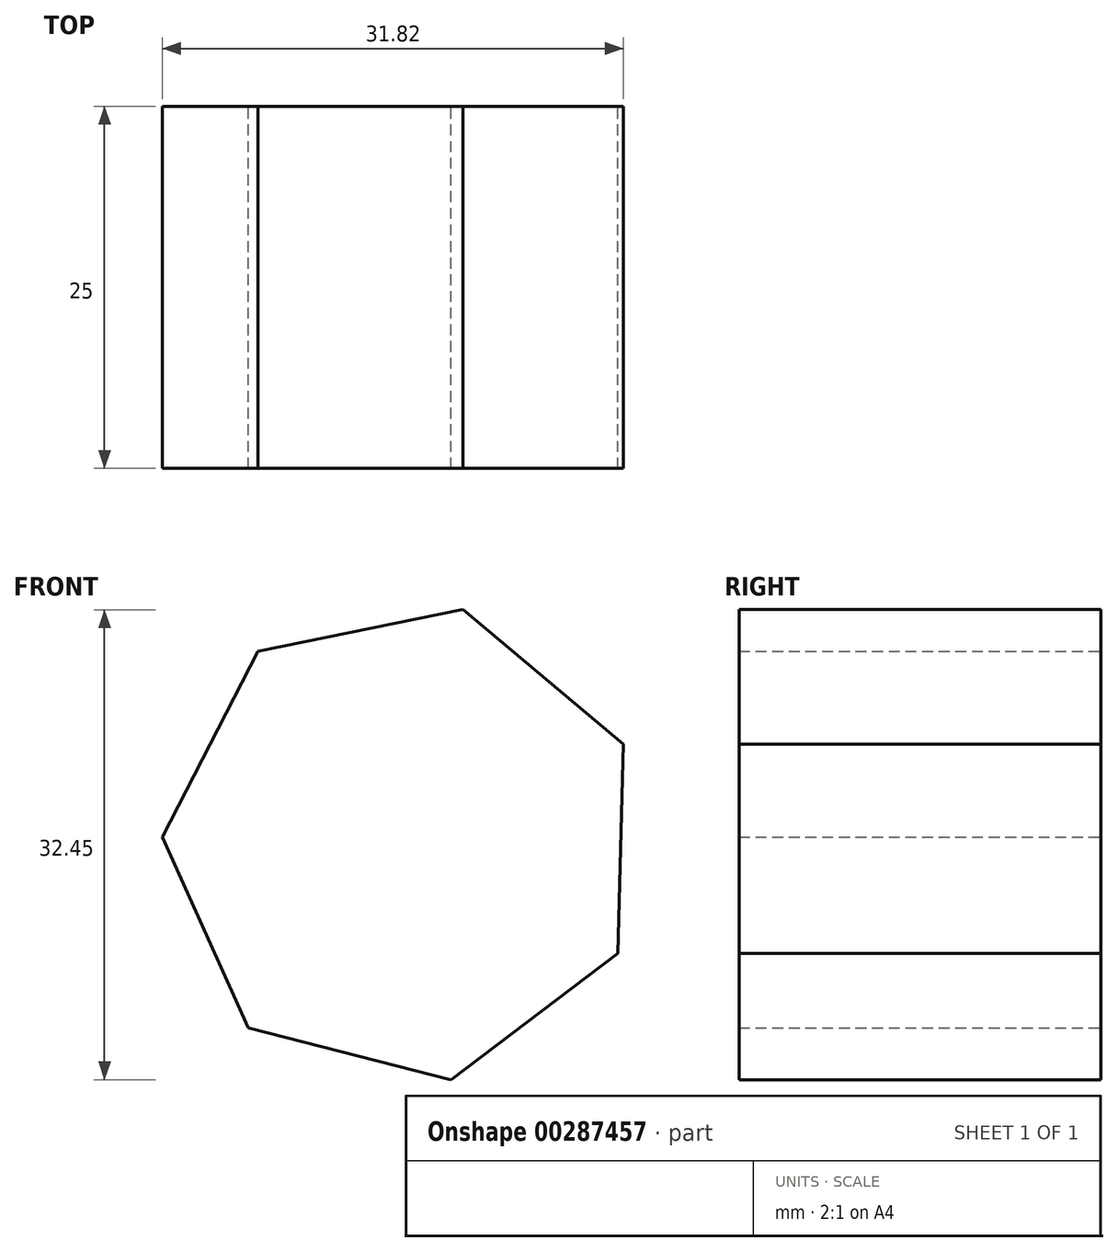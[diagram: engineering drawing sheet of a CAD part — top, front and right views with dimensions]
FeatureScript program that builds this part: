
annotation { "Feature Type Name" : "Feature", "Feature Type Description" : "" }
export const myFeature = defineFeature(function(context is Context, id is Id, definition is map)
    precondition{}
    {
        {
            var Q0;
            Q0=qCreatedBy(makeId("Front.planeOp"),FACE);
            var sketch = newSketch(context, id + "F0", { "sketchPlane" : qUnion([Q0])});
            skCircle(sketch, "E0.cCircle", {"center": v(0, 0) * mm, "radius": 15 * mm, "construction": true});
            skLineSegment(sketch, "E0.0", {"start": v(4.1, 16.13) * mm, "end": v(15.18, 6.85) * mm});
            skLineSegment(sketch, "E0.1", {"start": v(15.18, 6.85) * mm, "end": v(14.81, -7.6) * mm});
            skLineSegment(sketch, "E0.2", {"start": v(14.81, -7.6) * mm, "end": v(3.3, -16.32) * mm});
            skLineSegment(sketch, "E0.3", {"start": v(3.3, -16.32) * mm, "end": v(-10.7, -12.75) * mm});
            skLineSegment(sketch, "E0.4", {"start": v(-10.7, -12.75) * mm, "end": v(-16.64, 0.42) * mm});
            skLineSegment(sketch, "E0.5", {"start": v(-16.64, 0.42) * mm, "end": v(-10.05, 13.27) * mm});
            skLineSegment(sketch, "E0.6", {"start": v(-10.05, 13.27) * mm, "end": v(4.1, 16.13) * mm});
            skPoint(sketch, "E0.0.midPoint", {"position": v(9.64, 11.49) * mm});
            skSolve(sketch);
        }
        {
            var Q0;
            Q0=makeQuery(id+"F0.imprint","IMPRINT",FACE,{"disambiguationData":[TD([[makeQuery(id+"F0.imprint","IMPRINT",EDGE,{"derivedFrom":sQuery(id+"F0.wireOp",EDGE,"E0.0")}),-1.0]])]});
            extrude(context, id + "F1", {"entities" : qUnion([Q0]), "depth" : 25 * mm});
        }
    });
